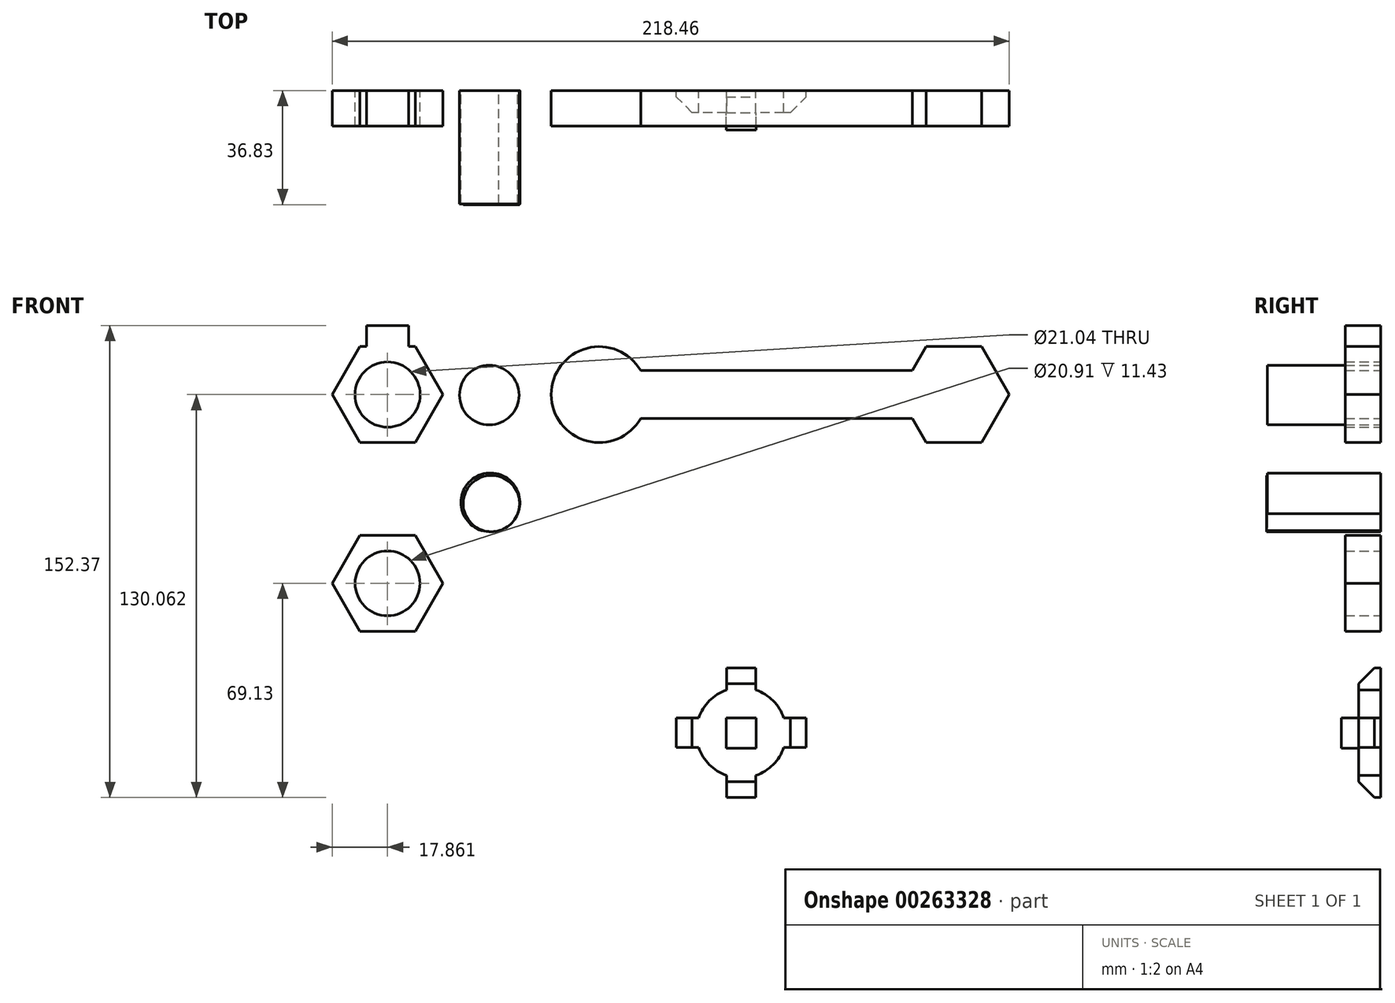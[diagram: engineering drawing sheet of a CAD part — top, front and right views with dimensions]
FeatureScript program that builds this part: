
annotation { "Feature Type Name" : "Feature", "Feature Type Description" : "" }
export const myFeature = defineFeature(function(context is Context, id is Id, definition is map)
    precondition{}
    {
        {
            var Q0;
            Q0=qCreatedBy(makeId("Front.planeOp"),FACE);
            var sketch = newSketch(context, id + "F0", { "sketchPlane" : qUnion([Q0])});
            skCircle(sketch, "E0.cCircle", {"center": v(-68.29, 60.93) * mm, "radius": 15.47 * mm, "construction": true});
            skLineSegment(sketch, "E0.0", {"start": v(-77.22, 76.4) * mm, "end": v(-59.36, 76.4) * mm});
            skLineSegment(sketch, "E0.1", {"start": v(-59.36, 76.4) * mm, "end": v(-50.43, 60.93) * mm});
            skLineSegment(sketch, "E0.2", {"start": v(-50.43, 60.93) * mm, "end": v(-59.36, 45.46) * mm});
            skLineSegment(sketch, "E0.3", {"start": v(-59.36, 45.46) * mm, "end": v(-77.22, 45.46) * mm});
            skLineSegment(sketch, "E0.4", {"start": v(-77.22, 45.46) * mm, "end": v(-86.15, 60.93) * mm});
            skLineSegment(sketch, "E0.5", {"start": v(-86.15, 60.93) * mm, "end": v(-77.22, 76.4) * mm});
            skPoint(sketch, "E0.0.midPoint", {"position": v(-68.29, 76.4) * mm});
            skCircle(sketch, "E1", {"center": v(-68.29, 60.93) * mm, "radius": 10.52 * mm});
            skCircle(sketch, "E2.cCircle", {"center": v(0, 60.93) * mm, "radius": 15.47 * mm, "construction": true});
            skPoint(sketch, "E2.0.midPoint", {"position": v(0, 76.4) * mm});
            skPoint(sketch, "E3.oppositeSnap0", {"position": v(13.4, 53.2) * mm});
            skLineSegment(sketch, "E3.bottom", {"start": v(13.4, 68.67) * mm, "end": v(114.45, 68.67) * mm});
            skLineSegment(sketch, "E3.top", {"start": v(13.4, 53.2) * mm, "end": v(114.45, 53.2) * mm});
            skLineSegment(sketch, "E3.left", {"start": v(13.4, 68.67) * mm, "end": v(13.4, 53.2) * mm});
            skLineSegment(sketch, "E3.right", {"start": v(114.45, 68.67) * mm, "end": v(114.45, 53.2) * mm});
            skCircle(sketch, "E4.cCircle", {"center": v(114.45, 60.93) * mm, "radius": 15.47 * mm, "construction": true});
            skLineSegment(sketch, "E4.0", {"start": v(105.52, 76.4) * mm, "end": v(123.38, 76.4) * mm});
            skLineSegment(sketch, "E4.1", {"start": v(123.38, 76.4) * mm, "end": v(132.31, 60.93) * mm});
            skLineSegment(sketch, "E4.2", {"start": v(132.31, 60.93) * mm, "end": v(123.38, 45.46) * mm});
            skLineSegment(sketch, "E4.3", {"start": v(123.38, 45.46) * mm, "end": v(105.52, 45.46) * mm});
            skLineSegment(sketch, "E4.4", {"start": v(105.52, 45.46) * mm, "end": v(96.6, 60.93) * mm});
            skLineSegment(sketch, "E4.5", {"start": v(96.6, 60.93) * mm, "end": v(105.52, 76.4) * mm});
            skPoint(sketch, "E4.0.midPoint", {"position": v(114.45, 76.4) * mm});
            skCircle(sketch, "E5", {"center": v(0, 60.93) * mm, "radius": 15.47 * mm});
            skCircle(sketch, "E6.cCircle", {"center": v(-68.29, 0) * mm, "radius": 15.47 * mm, "construction": true});
            skPoint(sketch, "E6.cCircle.centerSnap0", {"position": v(-68.29, 45.46) * mm});
            skPoint(sketch, "E6.cCircle.perimeterSnap0", {"position": v(-54.9, 53.2) * mm});
            skLineSegment(sketch, "E6.0", {"start": v(-50.43, 0) * mm, "end": v(-59.36, -15.47) * mm});
            skLineSegment(sketch, "E6.1", {"start": v(-59.36, -15.47) * mm, "end": v(-77.22, -15.47) * mm});
            skLineSegment(sketch, "E6.2", {"start": v(-77.22, -15.47) * mm, "end": v(-86.15, 0) * mm});
            skLineSegment(sketch, "E6.3", {"start": v(-86.15, 0) * mm, "end": v(-77.22, 15.47) * mm});
            skLineSegment(sketch, "E6.4", {"start": v(-77.22, 15.47) * mm, "end": v(-59.36, 15.47) * mm});
            skLineSegment(sketch, "E6.5", {"start": v(-59.36, 15.47) * mm, "end": v(-50.43, 0) * mm});
            skPoint(sketch, "E6.0.midPoint", {"position": v(-54.9, -7.73) * mm});
            skPoint(sketch, "E6.0.midPoint.positionSnap0", {"position": v(-54.9, 53.2) * mm});
            skCircle(sketch, "E7", {"center": v(-68.29, 0) * mm, "radius": 10.46 * mm});
            skLineSegment(sketch, "E8.0", {"start": v(-75.12, 83.24) * mm, "end": v(-61.45, 83.24) * mm});
            skLineSegment(sketch, "E8.1", {"start": v(-61.45, 83.24) * mm, "end": v(-61.45, 69.56) * mm});
            skLineSegment(sketch, "E8.3", {"start": v(-75.12, 69.56) * mm, "end": v(-75.12, 83.24) * mm});
            skPoint(sketch, "E8.0.midPoint", {"position": v(-68.29, 83.24) * mm});
            skLineSegment(sketch, "E9", {"start": v(-75.12, 69.56) * mm, "end": v(-68.29, 76.4) * mm});
            skLineSegment(sketch, "E10", {"start": v(-61.45, 69.56) * mm, "end": v(-68.29, 76.4) * mm});
            skSolve(sketch);
        }
        {
            var Q0;
            Q0 = qSketchRegion(id + "F0", true);
            extrude(context, id + "F1", {"entities" : qUnion([Q0]), "depth" : 11.43 * mm});
        }
        {
            var Q0;
            Q0=qCreatedBy(makeId("Front.planeOp"),FACE);
            var sketch = newSketch(context, id + "F2", { "sketchPlane" : qUnion([Q0])});
            skCircle(sketch, "E11", {"center": v(-35.1, 26.12) * mm, "radius": 9.5 * mm});
            skCircle(sketch, "E12", {"center": v(-35.46, 60.76) * mm, "radius": 9.62 * mm});
            skSolve(sketch);
        }
        {
            var Q0;
            Q0 = qSketchRegion(id + "F2", true);
            extrude(context, id + "F3", {"entities" : qUnion([Q0]), "depth" : 36.58 * mm});
        }
        {
            var Q0;
            Q0=qCreatedBy(makeId("Front.planeOp"),FACE);
            var sketch = newSketch(context, id + "F4", { "sketchPlane" : qUnion([Q0])});
            skCircle(sketch, "E13", {"center": v(45.85, -48.2) * mm, "radius": 14.56 * mm});
            skLineSegment(sketch, "E14.bottom", {"start": v(45.85, -48.2) * mm, "end": v(45.85, -48.2) * mm});
            skLineSegment(sketch, "E14.top", {"start": v(45.85, -62.76) * mm, "end": v(45.85, -62.76) * mm});
            skLineSegment(sketch, "E15.top", {"start": v(45.85, -33.64) * mm, "end": v(45.85, -33.64) * mm});
            skLineSegment(sketch, "E16.right", {"start": v(60.42, -48.2) * mm, "end": v(60.42, -48.2) * mm});
            skLineSegment(sketch, "E17.right", {"start": v(31.3, -48.2) * mm, "end": v(31.3, -48.2) * mm});
            skPoint(sketch, "E18.0.midPoint", {"position": v(45.85, -69.13) * mm});
            skLineSegment(sketch, "E19.bottom", {"start": v(66.78, -52.96) * mm, "end": v(24.92, -52.96) * mm});
            skLineSegment(sketch, "E19.top", {"start": v(66.78, -43.43) * mm, "end": v(24.92, -43.43) * mm});
            skLineSegment(sketch, "E19.left", {"start": v(66.78, -52.96) * mm, "end": v(66.78, -43.43) * mm});
            skLineSegment(sketch, "E19.right", {"start": v(24.92, -52.96) * mm, "end": v(24.92, -43.43) * mm});
            skLineSegment(sketch, "E20.bottom", {"start": v(41.11, -69.13) * mm, "end": v(50.6, -69.13) * mm});
            skLineSegment(sketch, "E20.top", {"start": v(41.11, -27.27) * mm, "end": v(50.6, -27.27) * mm});
            skLineSegment(sketch, "E20.left", {"start": v(41.11, -69.13) * mm, "end": v(41.11, -27.27) * mm});
            skLineSegment(sketch, "E20.right", {"start": v(50.6, -69.13) * mm, "end": v(50.6, -27.27) * mm});
            skSolve(sketch);
        }
        {
            var Q0;
            Q0 = qSketchRegion(id + "F4", true);
            extrude(context, id + "F5", {"entities" : qUnion([Q0]), "depth" : 7.11 * mm});
        }
        {
            var Q0;
            Q0=makeQuery(id+"F5.opExtrude","CAP_EDGE",EDGE,{"disambiguationData":[OSD([sQuery(id+"F4.wireOp",EDGE,"E20.top")])],"isStart":false});
            var Q1;
            Q1=makeQuery(id+"F5.opExtrude","CAP_EDGE",EDGE,{"disambiguationData":[OSD([sQuery(id+"F4.wireOp",EDGE,"E19.left")])],"isStart":false});
            var Q2;
            Q2=makeQuery(id+"F5.opExtrude","CAP_EDGE",EDGE,{"disambiguationData":[OSD([sQuery(id+"F4.wireOp",EDGE,"E20.bottom")])],"isStart":false});
            var Q3;
            Q3=makeQuery(id+"F5.opExtrude","CAP_EDGE",EDGE,{"disambiguationData":[OSD([sQuery(id+"F4.wireOp",EDGE,"E19.right")])],"isStart":false});
            var Q4;
            {var subQ0=sQuery(id+"F4.wireOp",EDGE,"E13");Q4=makeQuery(id+"F5.opExtrude","CAP_EDGE",EDGE,{"disambiguationData":[OSD([subQ0]),TDD([makeQuery(id+"F4.imprint","IMPRINT",EDGE,{"disambiguationData":[TD([[makeQuery(id+"F4.imprint","INTERSECT",VERTEX,{"disambiguationData":[OD(0.0)],"derivedFrom":[subQ0,sQuery(id+"F4.wireOp",EDGE,"E20.right")]}),1.0]])],"derivedFrom":subQ0})])],"isStart":false});}
            var Q5;
            {var subQ0=sQuery(id+"F4.wireOp",EDGE,"E13");Q5=makeQuery(id+"F5.opExtrude","CAP_EDGE",EDGE,{"disambiguationData":[OSD([subQ0]),TDD([makeQuery(id+"F4.imprint","IMPRINT",EDGE,{"disambiguationData":[TD([[makeQuery(id+"F4.imprint","INTERSECT",VERTEX,{"disambiguationData":[OD(1.0)],"derivedFrom":[subQ0,sQuery(id+"F4.wireOp",EDGE,"E20.right")]}),-1.0]])],"derivedFrom":subQ0})])],"isStart":false});}
            var Q6;
            {var subQ0=sQuery(id+"F4.wireOp",EDGE,"E13");Q6=makeQuery(id+"F5.opExtrude","CAP_EDGE",EDGE,{"disambiguationData":[OSD([subQ0]),TDD([makeQuery(id+"F4.imprint","IMPRINT",EDGE,{"disambiguationData":[TD([[makeQuery(id+"F4.imprint","INTERSECT",VERTEX,{"disambiguationData":[OD(0.0)],"derivedFrom":[subQ0,sQuery(id+"F4.wireOp",EDGE,"E20.left")]}),-1.0]])],"derivedFrom":subQ0})])],"isStart":false});}
            var Q7;
            {var subQ0=sQuery(id+"F4.wireOp",EDGE,"E13");Q7=makeQuery(id+"F5.opExtrude","CAP_EDGE",EDGE,{"disambiguationData":[OSD([subQ0]),TDD([makeQuery(id+"F4.imprint","IMPRINT",EDGE,{"disambiguationData":[TD([[makeQuery(id+"F4.imprint","INTERSECT",VERTEX,{"disambiguationData":[OD(0.0)],"derivedFrom":[subQ0,sQuery(id+"F4.wireOp",EDGE,"E19.bottom")]}),-1.0]])],"derivedFrom":subQ0})])],"isStart":false});}
            chamfer(context, id + "F6", {"entities" : qUnion([Q0, Q1, Q2, Q3, Q4, Q5, Q6, Q7]), "width" : 5.08 * mm, "tangentPropagation" : true});
        }
        {
            var Q0;
            Q0=qCreatedBy(makeId("Front.planeOp"),FACE);
            var sketch = newSketch(context, id + "F7", { "sketchPlane" : qUnion([Q0])});
            skLineSegment(sketch, "E21.bottom", {"start": v(50.66, -43.4) * mm, "end": v(40.95, -43.4) * mm});
            skLineSegment(sketch, "E21.top", {"start": v(50.66, -53.23) * mm, "end": v(40.95, -53.23) * mm});
            skLineSegment(sketch, "E21.left", {"start": v(50.66, -43.4) * mm, "end": v(50.66, -53.23) * mm});
            skLineSegment(sketch, "E21.right", {"start": v(40.95, -43.4) * mm, "end": v(40.95, -53.23) * mm});
            skSolve(sketch);
        }
        {
            var Q0;
            Q0 = qSketchRegion(id + "F7", true);
            extrude(context, id + "F8", {"entities" : qUnion([Q0]), "operationType" : NewBodyOperationType.ADD, "depth" : 12.7 * mm});
        }
        {
            var Q0;
            Q0=qCreatedBy(makeId("Front.planeOp"),FACE);
            var sketch = newSketch(context, id + "F9", { "sketchPlane" : qUnion([Q0])});
            skCircle(sketch, "E22", {"center": v(-34.77, 25.77) * mm, "radius": 9.08 * mm});
            skSolve(sketch);
        }
        {
            var Q0;
            Q0 = qSketchRegion(id + "F9", true);
            extrude(context, id + "F10", {"entities" : qUnion([Q0]), "operationType" : NewBodyOperationType.ADD, "depth" : 36.83 * mm});
        }
    });
